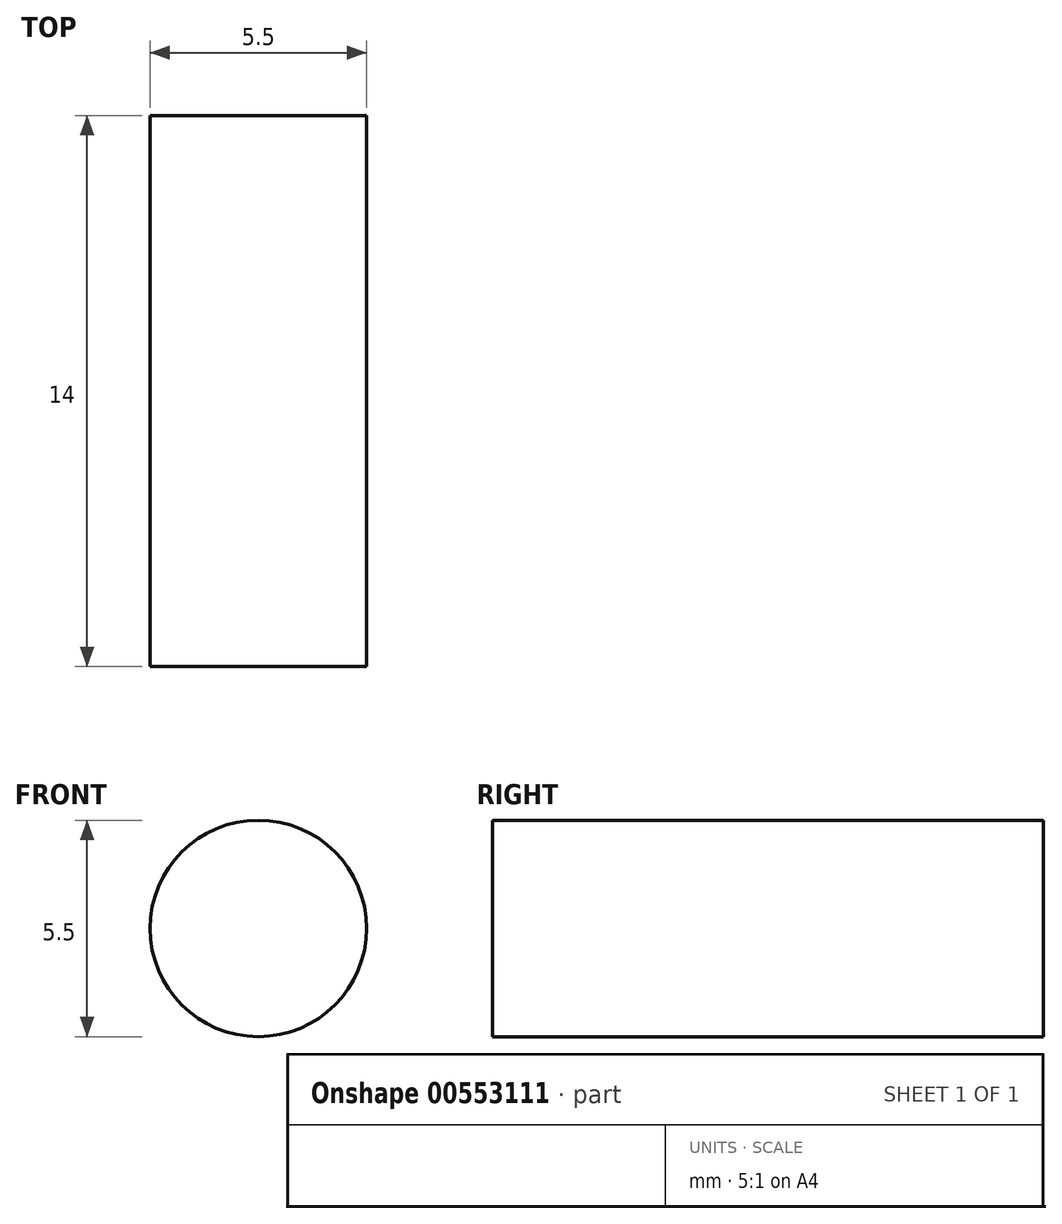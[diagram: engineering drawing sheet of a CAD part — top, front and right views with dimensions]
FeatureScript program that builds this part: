
annotation { "Feature Type Name" : "Feature", "Feature Type Description" : "" }
export const myFeature = defineFeature(function(context is Context, id is Id, definition is map)
    precondition{}
    {
        {
            var Q0;
            Q0=qCreatedBy(makeId("Front.planeOp"),FACE);
            var sketch = newSketch(context, id + "F0", { "sketchPlane" : qUnion([Q0])});
            skCircle(sketch, "E0", {"center": v(0, 0) * mm, "radius": 2.75 * mm});
            skSolve(sketch);
        }
        {
            var Q0;
            Q0 = qSketchRegion(id + "F0", true);
            extrude(context, id + "F1", {"entities" : qUnion([Q0]), "endBound" : BoundingType.SYMMETRIC, "depth" : 14 * mm, "offsetDistance" : 25 * mm});
        }
    });
